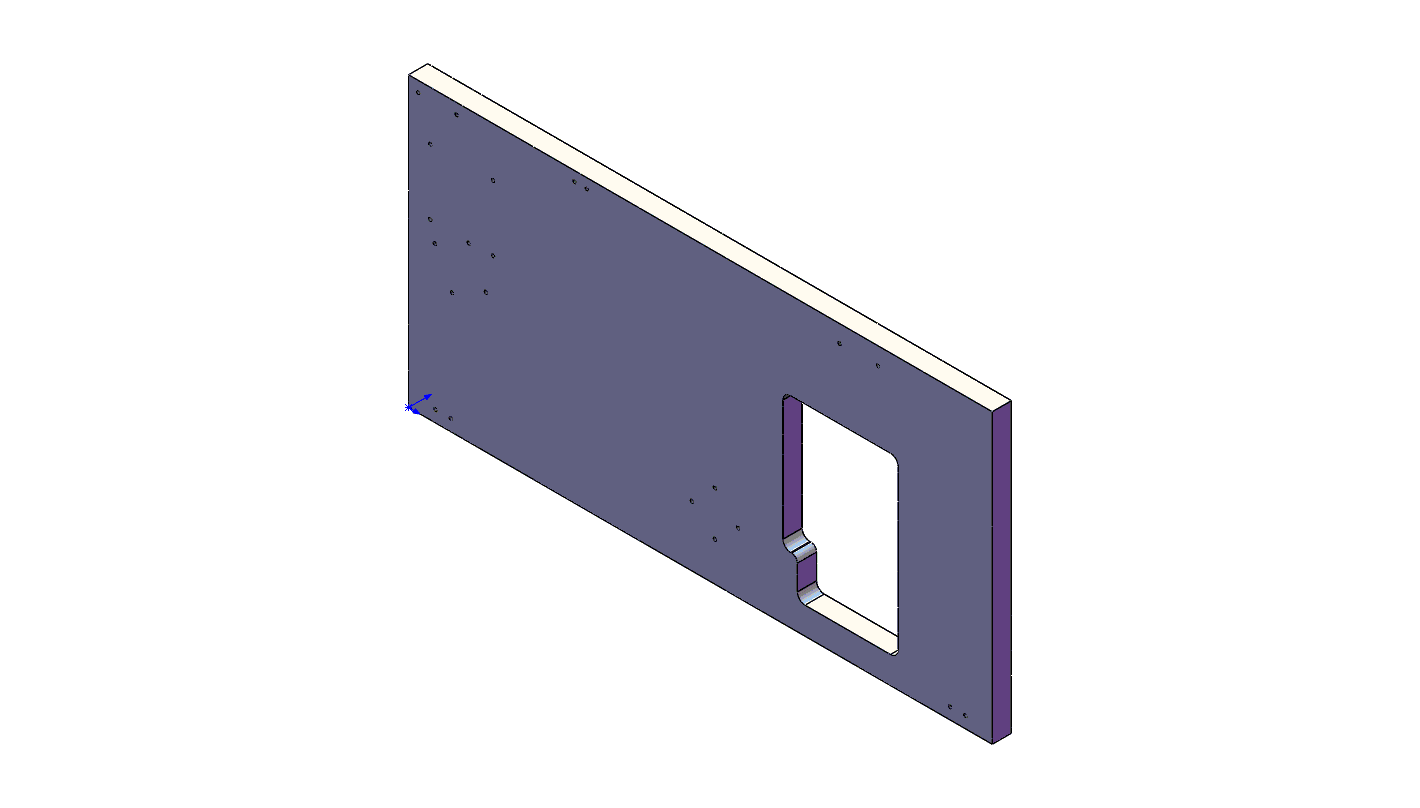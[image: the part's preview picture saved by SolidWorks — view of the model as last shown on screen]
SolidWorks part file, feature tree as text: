
SOLIDWORKS PART (.sldprt)
format: sldprt  version: not decoded by parser v0  size: 451,584 bytes
history: native  units: mm
features: thread x23, sketch x4, plane x3, extrude x2, material x1, hole x1 (+8 scaffold rows collapsed)
feature tree (42):
  scaffold x8  (default folders/planes/origin — collapsed)
  material  "AlMgSi0,5 (3.3206)"
  plane  "Draufsicht"
  plane  "Vorderansicht"
  plane  "Seitenansicht"
  sketch  "Skizze3"  dims[c1.D8=20.0mm c1.D9=15.0mm c1.D10=20.0mm c1.D1=0.0mm c1.D2=750.0mm c1.D3=0.0mm c1.D4=1520.0mm c2.D2=750.0mm c2.D1=1520.0mm c3.D2=750.0mm c3.D3=70.0mm c3.D4=~959.603828mm c3.D5=37.5mm c3.D6=300.0mm c3.D7=454.0mm c4.D4=975.0mm c4.D11=170.0mm]
  extrude  "Aufsatz-Linear austragen1"  Depth=50mm
  sketch  "Bohrungen"  dims[D1=0.0mm D2=25.0mm D3=100.0mm D4=125.0mm D5=464.0mm D6=432.0mm D7=717.5mm D8=740.0mm D9=780.0mm D10=802.5mm D11=1122.5mm D12=1222.5mm D13=1500.0mm D14=1520.0mm D15=540.0mm D16=760.0mm D17=835.0mm D18=1020.0mm D19=945.0mm D20=1025.0mm D21=1175.0mm D22=1215.0mm D23=1447.5mm D24=0.0mm D25=60.0mm D26=70.0mm D27=56.5mm D28=56.5mm D29=~68.426044mm D30=79.0mm D31=~113.36881mm D32=60.0mm D33=110.0mm D34=135.0mm D35=~156.63119mm D36=220.0mm D37=220.0mm D38=187.6mm D39=191.0mm D40=~197.323956mm D41=~201.573956mm D42=440.0mm D43=500.0mm D44=500.0mm D45=480.0mm D46=~737.853679mm D47=725.0mm D48=740.0mm D49=870.0mm D50=~797.853679mm D51=780.0mm D52=942.0mm D53=~857.853679mm D54=900.0mm D55=997.5mm D56=1020.0mm D57=1175.0mm D58=1297.5mm D59=1308.0mm D60=1335.0mm D61=1308.0mm D62=1372.5mm D63=1410.0mm D64=1460.0mm D65=1460.0mm D66=1450.0mm D67=1500.0mm D68=1520.0mm]
  extrude  "AusrichtungGruppe4"  [1 undecoded]
  hole  "M10 Gewindebohrung1"  Diameter=8.5mm Depth=50mm
  sketch  "Skizze17"
  sketch  "Skizze16"  dims[hole-wizard template sketch: 59 standard entries collapsed; hole parameters kept: c18.Bohrerdurchmesser=8.5mm c18.Bohrungstiefe=50.0mm]
  thread  "Bohrungsgewinde1"  Diameter=10mm  [1 undecoded]
  thread  "Bohrungsgewinde2"  Diameter=10mm  [1 undecoded]
  thread  "Bohrungsgewinde3"  Diameter=10mm  [1 undecoded]
  thread  "Bohrungsgewinde4"  Diameter=10mm  [1 undecoded]
  thread  "Bohrungsgewinde5"  Diameter=10mm  [1 undecoded]
  thread  "Bohrungsgewinde9"  Diameter=10mm  [1 undecoded]
  thread  "Bohrungsgewinde10"  Diameter=10mm  [1 undecoded]
  thread  "Bohrungsgewinde11"  Diameter=10mm  [1 undecoded]
  thread  "Bohrungsgewinde12"  Diameter=10mm  [1 undecoded]
  thread  "Bohrungsgewinde13"  Diameter=10mm  [1 undecoded]
  thread  "Bohrungsgewinde14"  Diameter=10mm  [1 undecoded]
  thread  "Bohrungsgewinde15"  Diameter=10mm  [1 undecoded]
  thread  "Bohrungsgewinde19"  Diameter=10mm  [1 undecoded]
  thread  "Bohrungsgewinde20"  Diameter=10mm  [1 undecoded]
  thread  "Bohrungsgewinde21"  Diameter=10mm  [1 undecoded]
  thread  "Bohrungsgewinde23"  Diameter=10mm  [1 undecoded]
  thread  "Bohrungsgewinde24"  Diameter=10mm  [1 undecoded]
  thread  "Bohrungsgewinde25"  Diameter=10mm  [1 undecoded]
  thread  "Bohrungsgewinde26"  Diameter=10mm  [1 undecoded]
  thread  "Bohrungsgewinde44"  Diameter=10mm  [1 undecoded]
  thread  "Bohrungsgewinde45"  Diameter=10mm  [1 undecoded]
  thread  "Bohrungsgewinde46"  Diameter=10mm  [1 undecoded]
  thread  "Bohrungsgewinde49"  Diameter=10mm  [1 undecoded]
decode coverage: 28 of 30 modeling features carry decoded parameters
note: ~ marks probable driven/reference dimensions
note: 24 parameter values undecoded
note: suppression state not decoded; provenance and decode notes live in map.json
